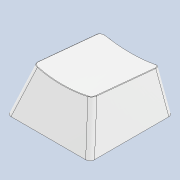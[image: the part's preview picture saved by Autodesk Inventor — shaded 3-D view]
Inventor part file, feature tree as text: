
AUTODESK INVENTOR PART (.ipt)
format: ipt  version: 2021 (Build 250183000, 183)  size: 249,856 bytes
history: native  units: in
note: dims shown in document units (in); Inventor stores cm internally (conversion verified against a paired STEP export)
features: chamfer x1
ambient origin geometry x8: Origin, YZ Plane, XZ Plane, XY Plane, X Axis, Y Axis, Z Axis, Center Point
bodies: Solid1 (feature_tree)
feature tree (1):
  chamfer  "Chamfer1"  [1 undecoded]
note: 1 required parameter value undecoded (feature->parameter linkage not recoverable at this tier; creation-order binding heuristic only, values carry confidence <= 0.55)
